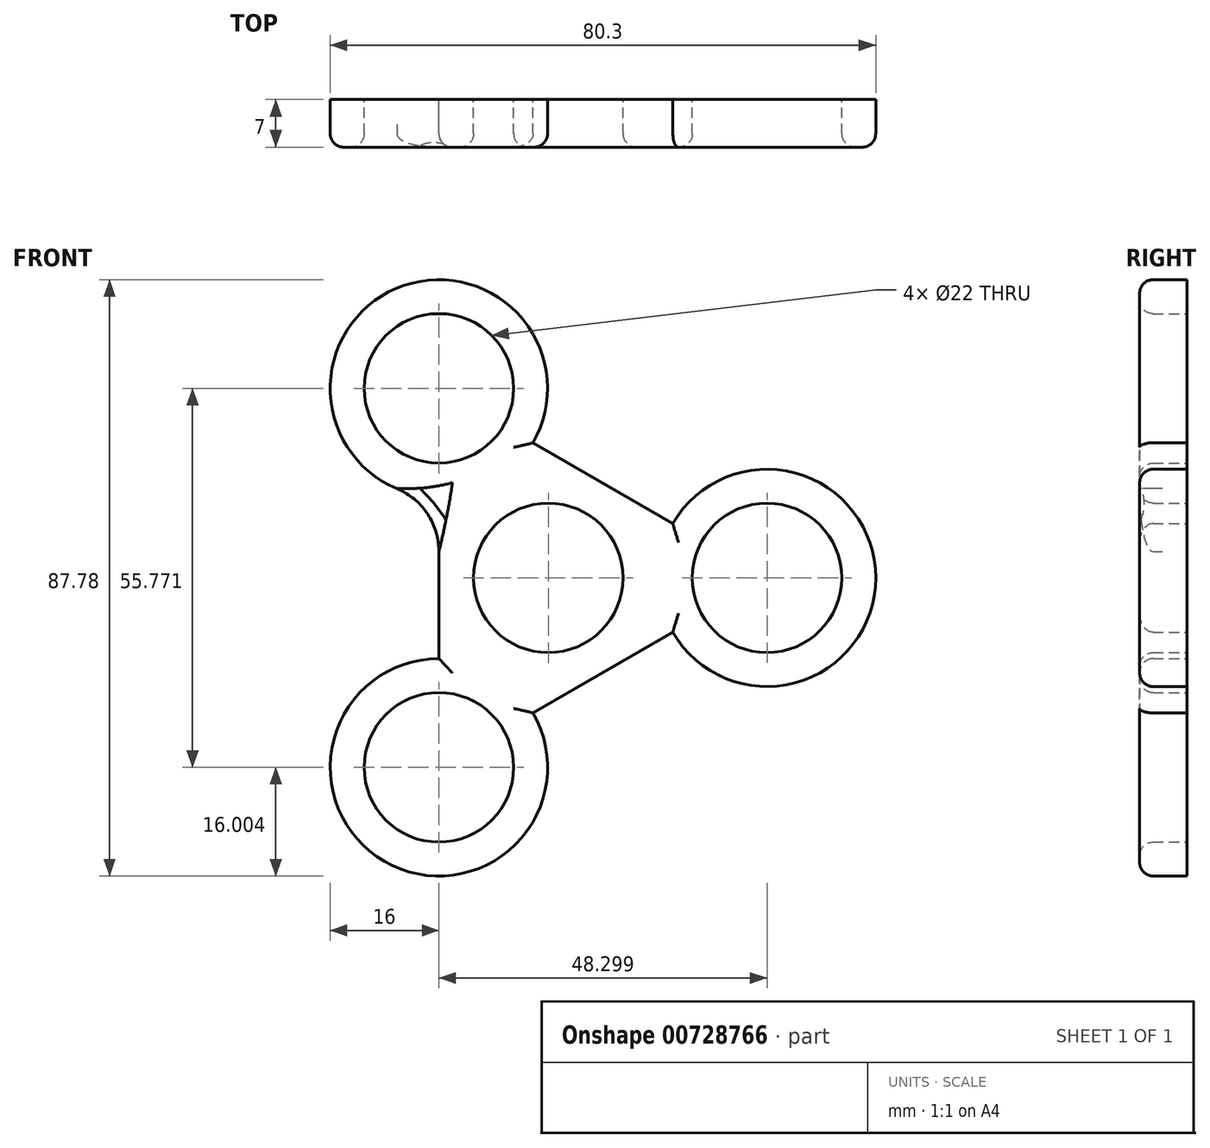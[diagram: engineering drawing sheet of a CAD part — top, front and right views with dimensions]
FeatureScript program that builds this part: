
annotation { "Feature Type Name" : "Feature", "Feature Type Description" : "" }
export const myFeature = defineFeature(function(context is Context, id is Id, definition is map)
    precondition{}
    {
        {
            var Q0;
            Q0=qCreatedBy(makeId("Front.planeOp"),FACE);
            var sketch = newSketch(context, id + "F0", { "sketchPlane" : qUnion([Q0])});
            skCircle(sketch, "E0", {"center": v(0, 0) * mm, "radius": 11 * mm});
            skCircle(sketch, "E1", {"center": v(32.2, 0) * mm, "radius": 11 * mm});
            skCircle(sketch, "E2", {"center": v(-16.1, 27.89) * mm, "radius": 11 * mm});
            skCircle(sketch, "E3", {"center": v(-16.1, -27.89) * mm, "radius": 11 * mm});
            skCircle(sketch, "E4.0", {"center": v(-16.1, -27.89) * mm, "radius": 16 * mm});
            skCircle(sketch, "E5.0", {"center": v(32.2, 0) * mm, "radius": 16 * mm});
            skCircle(sketch, "E6.0", {"center": v(-16.1, 27.89) * mm, "radius": 16 * mm});
            skCircle(sketch, "E7.0", {"center": v(0, 0) * mm, "radius": 16 * mm});
            skCircle(sketch, "E8.cCircle", {"center": v(0, 0) * mm, "radius": 32.2 * mm, "construction": true});
            skLineSegment(sketch, "E8.0", {"start": v(32.2, 0) * mm, "end": v(-16.1, -27.89) * mm});
            skLineSegment(sketch, "E8.1", {"start": v(-16.1, -27.89) * mm, "end": v(-16.1, 27.89) * mm});
            skLineSegment(sketch, "E8.2", {"start": v(-16.1, 27.89) * mm, "end": v(32.2, 0) * mm});
            skPoint(sketch, "E9.1.internal.snap0", {"position": v(-16.1, 0) * mm});
            skPoint(sketch, "E10", {"position": v(-27.53, 16.7) * mm});
            skPoint(sketch, "E11", {"position": v(-27.53, -16.7) * mm});
            skPoint(sketch, "E12", {"position": v(-0.7, -32.2) * mm});
            skPoint(sketch, "E13", {"position": v(28.22, -15.5) * mm});
            skPoint(sketch, "E14", {"position": v(28.22, 15.5) * mm});
            skPoint(sketch, "E15", {"position": v(-0.7, 32.2) * mm});
            skSolve(sketch);
        }
        {
            var Q0;
            {var subQ0=sQuery(id+"F0.wireOp",EDGE,"E8.0");var subQ1=sQuery(id+"F0.wireOp",EDGE,"E1");var subQ2=makeQuery(id+"F0.imprint","INTERSECT",VERTEX,{"derivedFrom":[subQ1,subQ0]});Q0=makeQuery(id+"F0.imprint","IMPRINT",FACE,{"disambiguationData":[TD([[makeQuery(id+"F0.imprint","IMPRINT",EDGE,{"disambiguationData":[TD([[subQ2,-1.0]])],"derivedFrom":subQ1}),-1.0]])]});}
            var Q1;
            {var subQ0=sQuery(id+"F0.wireOp",EDGE,"E8.1");var subQ1=sQuery(id+"F0.wireOp",EDGE,"E2");var subQ2=makeQuery(id+"F0.imprint","INTERSECT",VERTEX,{"derivedFrom":[subQ1,subQ0]});Q1=makeQuery(id+"F0.imprint","IMPRINT",FACE,{"disambiguationData":[TD([[makeQuery(id+"F0.imprint","IMPRINT",EDGE,{"disambiguationData":[TD([[subQ2,1.0]])],"derivedFrom":subQ1}),-1.0]])]});}
            var Q2;
            {var subQ0=sQuery(id+"F0.wireOp",EDGE,"E8.0");var subQ1=sQuery(id+"F0.wireOp",EDGE,"E3");var subQ2=makeQuery(id+"F0.imprint","INTERSECT",VERTEX,{"derivedFrom":[subQ1,subQ0]});Q2=makeQuery(id+"F0.imprint","IMPRINT",FACE,{"disambiguationData":[TD([[makeQuery(id+"F0.imprint","IMPRINT",EDGE,{"disambiguationData":[TD([[subQ2,1.0]])],"derivedFrom":subQ1}),-1.0]])]});}
            var Q3;
            {var subQ0=sQuery(id+"F0.wireOp",EDGE,"E8.0");var subQ1=sQuery(id+"F0.wireOp",EDGE,"E1");var subQ2=makeQuery(id+"F0.imprint","INTERSECT",VERTEX,{"derivedFrom":[subQ1,subQ0]});Q3=makeQuery(id+"F0.imprint","IMPRINT",FACE,{"disambiguationData":[TD([[makeQuery(id+"F0.imprint","IMPRINT",EDGE,{"disambiguationData":[TD([[subQ2,1.0]])],"derivedFrom":subQ1}),-1.0]])]});}
            var Q4;
            {var subQ0=sQuery(id+"F0.wireOp",EDGE,"E8.1");var subQ1=sQuery(id+"F0.wireOp",EDGE,"E2");var subQ2=makeQuery(id+"F0.imprint","INTERSECT",VERTEX,{"derivedFrom":[subQ1,subQ0]});Q4=makeQuery(id+"F0.imprint","IMPRINT",FACE,{"disambiguationData":[TD([[makeQuery(id+"F0.imprint","IMPRINT",EDGE,{"disambiguationData":[TD([[subQ2,-1.0]])],"derivedFrom":subQ1}),-1.0]])]});}
            var Q5;
            {var subQ0=sQuery(id+"F0.wireOp",EDGE,"E8.0");var subQ1=sQuery(id+"F0.wireOp",EDGE,"E3");var subQ2=makeQuery(id+"F0.imprint","INTERSECT",VERTEX,{"derivedFrom":[subQ1,subQ0]});Q5=makeQuery(id+"F0.imprint","IMPRINT",FACE,{"disambiguationData":[TD([[makeQuery(id+"F0.imprint","IMPRINT",EDGE,{"disambiguationData":[TD([[subQ2,-1.0]])],"derivedFrom":subQ1}),-1.0]])]});}
            var Q6;
            Q6=makeQuery(id+"F0.imprint","IMPRINT",FACE,{"disambiguationData":[TD([[makeQuery(id+"F0.imprint","IMPRINT",EDGE,{"derivedFrom":sQuery(id+"F0.wireOp",EDGE,"E0")}),-1.0]])]});
            var Q7;
            Q7=makeQuery(id+"F0.imprint","IMPRINT",FACE,{"disambiguationData":[TD([[makeQuery(id+"F0.imprint","IMPRINT",EDGE,{"derivedFrom":sQuery(id+"F0.wireOp",EDGE,"E7.0")}),-1.0]])]});
            extrude(context, id + "F1", {"entities" : qUnion([Q0, Q1, Q2, Q3, Q4, Q5, Q6, Q7]), "endBound" : BoundingType.SYMMETRIC, "depth" : 7 * mm, "offsetDistance" : 25 * mm});
        }
        {
            var Q0;
            Q0=makeQuery(id+"F1.opExtrude","CAP_EDGE",EDGE,{"disambiguationData":[OSD([sQuery(id+"F0.wireOp",EDGE,"E6.0")])],"isStart":false});
            var Q1;
            {var subQ0=sQuery(id+"F0.wireOp",EDGE,"bf94ace6-4371-4c62-abcf-97883a39ae37");Q1=makeQuery(id+"F1.opExtrude","CAP_EDGE",EDGE,{"disambiguationData":[OSD([subQ0]),TDD([makeQuery(id+"F0.imprint","IMPRINT",EDGE,{"disambiguationData":[TD([[makeQuery(id+"F0.imprint","INTERSECT",VERTEX,{"disambiguationData":[OD(1.0)],"derivedFrom":[sQuery(id+"F0.wireOp",EDGE,"E6.0"),subQ0]}),-1.0]])],"derivedFrom":subQ0})])],"isStart":false});}
            var Q2;
            {var subQ0=sQuery(id+"F0.wireOp",EDGE,"bf94ace6-4371-4c62-abcf-97883a39ae37");Q2=makeQuery(id+"F1.opExtrude","CAP_EDGE",EDGE,{"disambiguationData":[OSD([subQ0]),TDD([makeQuery(id+"F0.imprint","IMPRINT",EDGE,{"disambiguationData":[TD([[makeQuery(id+"F0.imprint","INTERSECT",VERTEX,{"disambiguationData":[OD(1.0)],"derivedFrom":[sQuery(id+"F0.wireOp",EDGE,"E5.0"),subQ0]}),1.0]])],"derivedFrom":subQ0})])],"isStart":false});}
            var Q3;
            Q3=makeQuery(id+"F1.opExtrude","CAP_EDGE",EDGE,{"disambiguationData":[OSD([sQuery(id+"F0.wireOp",EDGE,"E5.0")])],"isStart":false});
            var Q4;
            {var subQ0=sQuery(id+"F0.wireOp",EDGE,"454d4acc-7cbe-419e-8e68-d606df156991");Q4=makeQuery(id+"F1.opExtrude","CAP_EDGE",EDGE,{"disambiguationData":[OSD([subQ0]),TDD([makeQuery(id+"F0.imprint","IMPRINT",EDGE,{"disambiguationData":[TD([[makeQuery(id+"F0.imprint","INTERSECT",VERTEX,{"disambiguationData":[OD(1.0)],"derivedFrom":[sQuery(id+"F0.wireOp",EDGE,"E5.0"),subQ0]}),-1.0]])],"derivedFrom":subQ0})])],"isStart":false});}
            var Q5;
            {var subQ0=sQuery(id+"F0.wireOp",EDGE,"454d4acc-7cbe-419e-8e68-d606df156991");Q5=makeQuery(id+"F1.opExtrude","CAP_EDGE",EDGE,{"disambiguationData":[OSD([subQ0]),TDD([makeQuery(id+"F0.imprint","IMPRINT",EDGE,{"disambiguationData":[TD([[makeQuery(id+"F0.imprint","INTERSECT",VERTEX,{"disambiguationData":[OD(1.0)],"derivedFrom":[sQuery(id+"F0.wireOp",EDGE,"E4.0"),subQ0]}),1.0]])],"derivedFrom":subQ0})])],"isStart":false});}
            var Q6;
            Q6=makeQuery(id+"F1.opExtrude","CAP_EDGE",EDGE,{"disambiguationData":[OSD([sQuery(id+"F0.wireOp",EDGE,"E4.0")])],"isStart":false});
            var Q7;
            {var subQ0=sQuery(id+"F0.wireOp",EDGE,"E9");Q7=makeQuery(id+"F1.opExtrude","CAP_EDGE",EDGE,{"disambiguationData":[OSD([subQ0]),TDD([makeQuery(id+"F0.imprint","IMPRINT",EDGE,{"disambiguationData":[TD([[makeQuery(id+"F0.imprint","INTERSECT",VERTEX,{"disambiguationData":[OD(1.0)],"derivedFrom":[sQuery(id+"F0.wireOp",EDGE,"E4.0"),subQ0]}),1.0]])],"derivedFrom":subQ0})])],"isStart":false});}
            var Q8;
            {var subQ0=sQuery(id+"F0.wireOp",EDGE,"E9");Q8=makeQuery(id+"F1.opExtrude","CAP_EDGE",EDGE,{"disambiguationData":[OSD([subQ0]),TDD([makeQuery(id+"F0.imprint","IMPRINT",EDGE,{"disambiguationData":[TD([[makeQuery(id+"F0.imprint","INTERSECT",VERTEX,{"disambiguationData":[OD(1.0)],"derivedFrom":[sQuery(id+"F0.wireOp",EDGE,"E6.0"),subQ0]}),-1.0]])],"derivedFrom":subQ0})])],"isStart":false});}
            var Q9;
            Q9=makeQuery(id+"F1.opExtrude","CAP_FACE",FACE,{"disambiguationData":[OSD([sQuery(id+"F0.wireOp",EDGE,"E0"),sQuery(id+"F0.wireOp",EDGE,"E1"),sQuery(id+"F0.wireOp",EDGE,"E2"),sQuery(id+"F0.wireOp",EDGE,"E3"),sQuery(id+"F0.wireOp",EDGE,"E4.0"),sQuery(id+"F0.wireOp",EDGE,"E5.0"),sQuery(id+"F0.wireOp",EDGE,"E6.0"),sQuery(id+"F0.wireOp",EDGE,"E7.0"),sQuery(id+"F0.wireOp",EDGE,"E8.0"),sQuery(id+"F0.wireOp",EDGE,"E8.1"),sQuery(id+"F0.wireOp",EDGE,"E8.2"),sQuery(id+"F0.wireOp",EDGE,"E9"),sQuery(id+"F0.wireOp",EDGE,"bf94ace6-4371-4c62-abcf-97883a39ae37"),sQuery(id+"F0.wireOp",EDGE,"454d4acc-7cbe-419e-8e68-d606df156991")])],"isStart":false});
            fillet(context, id + "F2", {"entities" : qUnion([Q0, Q1, Q2, Q3, Q4, Q5, Q6, Q7, Q8, Q9]), "radius" : 2 * mm, "tangentPropagation" : true, "allowEdgeOverflow" : false});
        }
        {
            var Q0;
            Q0=makeQuery(id+"F1.opExtrude","SWEPT_EDGE",EDGE,{"disambiguationData":[OSD([sQuery(id+"F0.wireOp",EDGE,"E6.0"),sQuery(id+"F0.wireOp",EDGE,"E8.1")])]});
            fillet(context, id + "F3", {"entities" : qUnion([Q0]), "radius" : 10 * mm, "tangentPropagation" : true, "allowEdgeOverflow" : false});
        }
    });
